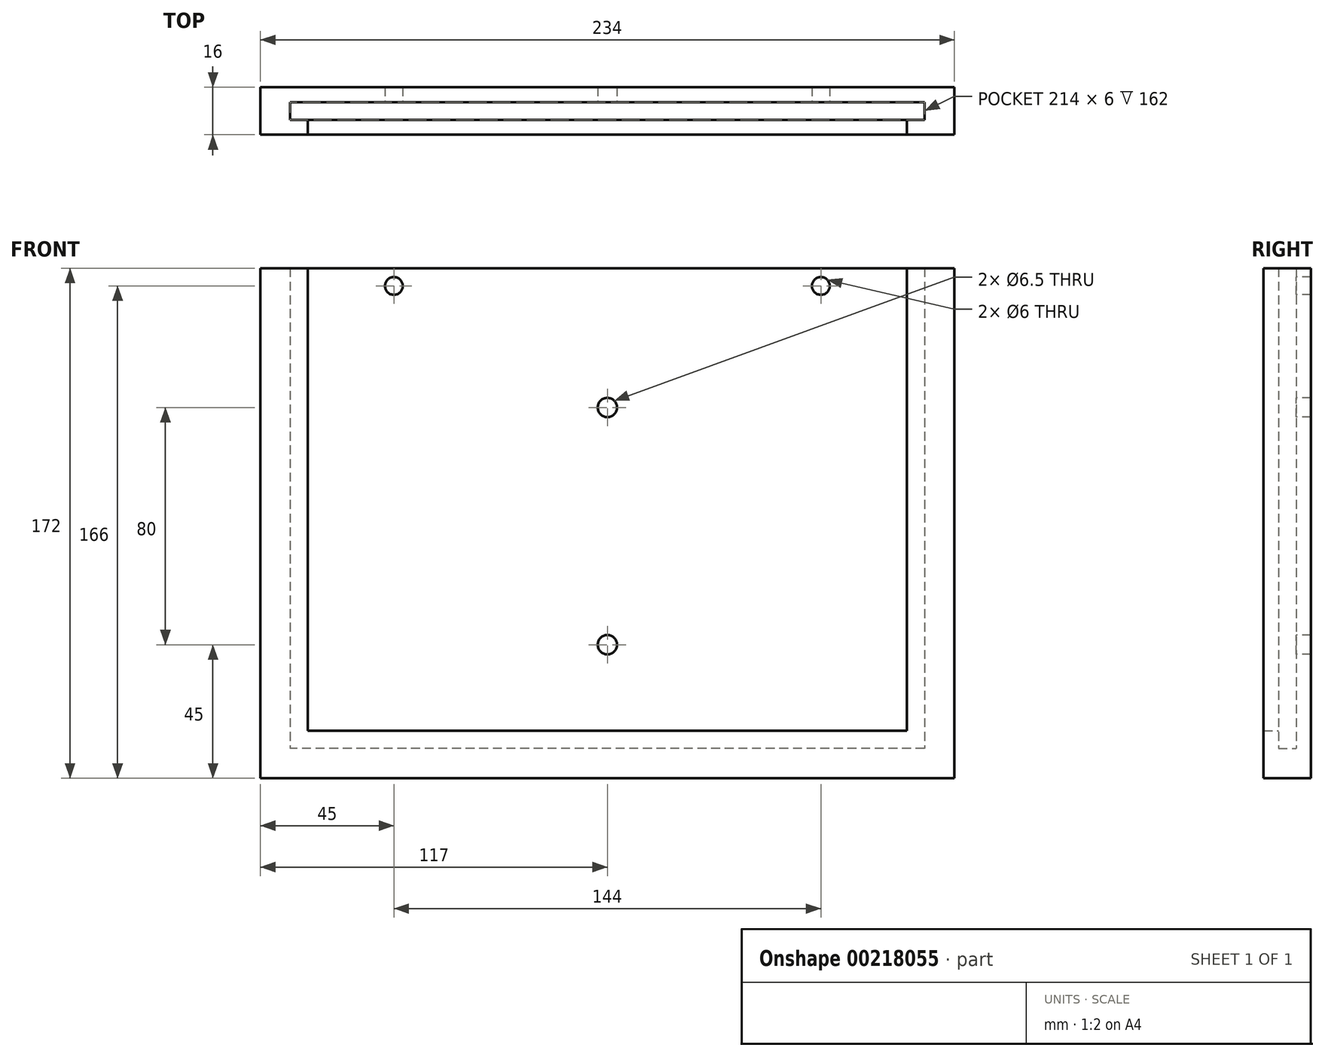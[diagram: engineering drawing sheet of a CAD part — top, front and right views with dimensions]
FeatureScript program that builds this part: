
annotation { "Feature Type Name" : "Feature", "Feature Type Description" : "" }
export const myFeature = defineFeature(function(context is Context, id is Id, definition is map)
    precondition{}
    {
        {
            var Q0;
            Q0=qCreatedBy(makeId("Top.planeOp"),FACE);
            var sketch = newSketch(context, id + "F0", { "sketchPlane" : qUnion([Q0])});
            skLineSegment(sketch, "E0.bottom", {"start": v(-117, 8) * mm, "end": v(117, 8) * mm});
            skLineSegment(sketch, "E0.top", {"start": v(-117, -8) * mm, "end": v(117, -8) * mm});
            skLineSegment(sketch, "E0.left", {"start": v(-117, 8) * mm, "end": v(-117, -8) * mm});
            skLineSegment(sketch, "E0.right", {"start": v(117, 8) * mm, "end": v(117, -8) * mm});
            skPoint(sketch, "E0.middle", {"position": v(0, 0) * mm});
            skLineSegment(sketch, "E1.top", {"start": v(-117, 3) * mm, "end": v(117, 3) * mm});
            skLineSegment(sketch, "E1.left", {"start": v(-117, 8) * mm, "end": v(-117, 3) * mm});
            skLineSegment(sketch, "E1.right", {"start": v(117, 8) * mm, "end": v(117, 3) * mm});
            skLineSegment(sketch, "E2", {"start": v(-107, -8) * mm, "end": v(-107, 8) * mm});
            skLineSegment(sketch, "E3", {"start": v(107, -8) * mm, "end": v(107, 8) * mm});
            skLineSegment(sketch, "E4.bottom", {"start": v(-117, -8) * mm, "end": v(-101, -8) * mm});
            skLineSegment(sketch, "E4.top", {"start": v(-117, -3) * mm, "end": v(-101, -3) * mm});
            skLineSegment(sketch, "E4.left", {"start": v(-117, -8) * mm, "end": v(-117, -3) * mm});
            skLineSegment(sketch, "E4.right", {"start": v(-101, -8) * mm, "end": v(-101, -3) * mm});
            skLineSegment(sketch, "E5.bottom", {"start": v(117, -8) * mm, "end": v(101, -8) * mm});
            skLineSegment(sketch, "E5.top", {"start": v(117, -3) * mm, "end": v(101, -3) * mm});
            skLineSegment(sketch, "E5.left", {"start": v(117, -8) * mm, "end": v(117, -3) * mm});
            skLineSegment(sketch, "E5.right", {"start": v(101, -8) * mm, "end": v(101, -3) * mm});
            skLineSegment(sketch, "E6.bottom", {"start": v(-101, -3) * mm, "end": v(107, -3) * mm});
            skLineSegment(sketch, "E6.top", {"start": v(-101, -8) * mm, "end": v(107, -8) * mm});
            skLineSegment(sketch, "E6.left", {"start": v(-101, -3) * mm, "end": v(-101, -8) * mm});
            skLineSegment(sketch, "E6.right", {"start": v(107, -3) * mm, "end": v(107, -8) * mm});
            skSolve(sketch);
        }
        {
            var Q0;
            {var subQ9=sQuery(id+"F0.wireOp",EDGE,"E6.bottom");Q0=makeQuery(id+"F0.imprint","IMPRINT",FACE,{"disambiguationData":[TD([[makeQuery(id+"F0.imprint","IMPRINT",EDGE,{"derivedFrom":subQ9}),1.0]])]});}
            var Q1;
            {var subQ0=sQuery(id+"F0.wireOp",EDGE,"E2");var subQ1=sQuery(id+"F0.wireOp",EDGE,"E0.bottom");var subQ2=makeQuery(id+"F0.imprint","INTERSECT",VERTEX,{"derivedFrom":[subQ1,subQ0]});Q1=makeQuery(id+"F0.imprint","IMPRINT",FACE,{"disambiguationData":[TD([[makeQuery(id+"F0.imprint","IMPRINT",EDGE,{"disambiguationData":[TD([[subQ2,-1.0]])],"derivedFrom":subQ1}),-1.0]])]});}
            var Q2;
            {var subQ0=sQuery(id+"F0.wireOp",EDGE,"E4.right");Q2=makeQuery(id+"F0.imprint","IMPRINT",FACE,{"disambiguationData":[TD([[makeQuery(id+"F0.imprint","IMPRINT",EDGE,{"derivedFrom":subQ0}),-1.0]])]});}
            var Q3;
            {var subQ0=sQuery(id+"F0.wireOp",EDGE,"E1.top");var subQ1=sQuery(id+"F0.wireOp",EDGE,"E0.left");var subQ2=makeQuery(id+"F0.imprint","INTERSECT",VERTEX,{"derivedFrom":[subQ1,subQ0]});Q3=makeQuery(id+"F0.imprint","IMPRINT",FACE,{"disambiguationData":[TD([[makeQuery(id+"F0.imprint","IMPRINT",EDGE,{"disambiguationData":[TD([[subQ2,-1.0]])],"derivedFrom":subQ1}),1.0]])]});}
            var Q4;
            {var subQ0=sQuery(id+"F0.wireOp",EDGE,"E2");var subQ1=sQuery(id+"F0.wireOp",EDGE,"E0.bottom");var subQ2=makeQuery(id+"F0.imprint","INTERSECT",VERTEX,{"derivedFrom":[subQ1,subQ0]});Q4=makeQuery(id+"F0.imprint","IMPRINT",FACE,{"disambiguationData":[TD([[makeQuery(id+"F0.imprint","IMPRINT",EDGE,{"disambiguationData":[TD([[subQ2,1.0]])],"derivedFrom":subQ1}),-1.0]])]});}
            var Q5;
            {var subQ0=sQuery(id+"F0.wireOp",EDGE,"E0.left");var subQ1=sQuery(id+"F0.wireOp",EDGE,"E0.top");var subQ2=makeQuery(id+"F0.imprint","INTERSECT",VERTEX,{"derivedFrom":[subQ1,subQ0]});Q5=makeQuery(id+"F0.imprint","IMPRINT",FACE,{"disambiguationData":[TD([[makeQuery(id+"F0.imprint","IMPRINT",EDGE,{"disambiguationData":[TD([[subQ2,-1.0]])],"derivedFrom":subQ1}),1.0]])]});}
            var Q6;
            {var subQ0=sQuery(id+"F0.wireOp",EDGE,"E4.right");Q6=makeQuery(id+"F0.imprint","IMPRINT",FACE,{"disambiguationData":[TD([[makeQuery(id+"F0.imprint","IMPRINT",EDGE,{"derivedFrom":subQ0}),1.0]])]});}
            var Q7;
            {var subQ0=sQuery(id+"F0.wireOp",EDGE,"E1.top");var subQ1=sQuery(id+"F0.wireOp",EDGE,"E0.right");var subQ2=makeQuery(id+"F0.imprint","INTERSECT",VERTEX,{"derivedFrom":[subQ1,subQ0]});Q7=makeQuery(id+"F0.imprint","IMPRINT",FACE,{"disambiguationData":[TD([[makeQuery(id+"F0.imprint","IMPRINT",EDGE,{"disambiguationData":[TD([[subQ2,-1.0]])],"derivedFrom":subQ1}),-1.0]])]});}
            var Q8;
            {var subQ0=sQuery(id+"F0.wireOp",EDGE,"E0.right");var subQ1=sQuery(id+"F0.wireOp",EDGE,"E0.bottom");var subQ2=makeQuery(id+"F0.imprint","INTERSECT",VERTEX,{"derivedFrom":[subQ1,subQ0]});Q8=makeQuery(id+"F0.imprint","IMPRINT",FACE,{"disambiguationData":[TD([[makeQuery(id+"F0.imprint","IMPRINT",EDGE,{"disambiguationData":[TD([[subQ2,1.0]])],"derivedFrom":subQ1}),-1.0]])]});}
            var Q9;
            {var subQ3=sQuery(id+"F0.wireOp",EDGE,"E5.right");Q9=makeQuery(id+"F0.imprint","IMPRINT",FACE,{"disambiguationData":[TD([[makeQuery(id+"F0.imprint","IMPRINT",EDGE,{"derivedFrom":subQ3}),-1.0]])]});}
            var Q10;
            {var subQ0=sQuery(id+"F0.wireOp",EDGE,"E3");var subQ1=sQuery(id+"F0.wireOp",EDGE,"E0.top");var subQ2=makeQuery(id+"F0.imprint","INTERSECT",VERTEX,{"derivedFrom":[subQ1,subQ0]});Q10=makeQuery(id+"F0.imprint","IMPRINT",FACE,{"disambiguationData":[TD([[makeQuery(id+"F0.imprint","IMPRINT",EDGE,{"disambiguationData":[TD([[subQ2,-1.0]])],"derivedFrom":subQ1}),1.0]])]});}
            extrude(context, id + "F1", {"entities" : qUnion([Q0, Q1, Q2, Q3, Q4, Q5, Q6, Q7, Q8, Q9, Q10]), "oppositeDirection" : true, "depth" : 10 * mm, "offsetDistance" : 25 * mm});
        }
        {
            var Q0;
            {var subQ0=sQuery(id+"F0.wireOp",EDGE,"E2");var subQ1=sQuery(id+"F0.wireOp",EDGE,"E0.bottom");var subQ2=makeQuery(id+"F0.imprint","INTERSECT",VERTEX,{"derivedFrom":[subQ1,subQ0]});Q0=makeQuery(id+"F0.imprint","IMPRINT",FACE,{"disambiguationData":[TD([[makeQuery(id+"F0.imprint","IMPRINT",EDGE,{"disambiguationData":[TD([[subQ2,-1.0]])],"derivedFrom":subQ1}),-1.0]])]});}
            var Q1;
            {var subQ0=sQuery(id+"F0.wireOp",EDGE,"E2");var subQ1=sQuery(id+"F0.wireOp",EDGE,"E0.bottom");var subQ2=makeQuery(id+"F0.imprint","INTERSECT",VERTEX,{"derivedFrom":[subQ1,subQ0]});Q1=makeQuery(id+"F0.imprint","IMPRINT",FACE,{"disambiguationData":[TD([[makeQuery(id+"F0.imprint","IMPRINT",EDGE,{"disambiguationData":[TD([[subQ2,1.0]])],"derivedFrom":subQ1}),-1.0]])]});}
            var Q2;
            {var subQ0=sQuery(id+"F0.wireOp",EDGE,"E1.top");var subQ1=sQuery(id+"F0.wireOp",EDGE,"E0.left");var subQ2=makeQuery(id+"F0.imprint","INTERSECT",VERTEX,{"derivedFrom":[subQ1,subQ0]});Q2=makeQuery(id+"F0.imprint","IMPRINT",FACE,{"disambiguationData":[TD([[makeQuery(id+"F0.imprint","IMPRINT",EDGE,{"disambiguationData":[TD([[subQ2,-1.0]])],"derivedFrom":subQ1}),1.0]])]});}
            var Q3;
            {var subQ0=sQuery(id+"F0.wireOp",EDGE,"E0.left");var subQ1=sQuery(id+"F0.wireOp",EDGE,"E0.top");var subQ2=makeQuery(id+"F0.imprint","INTERSECT",VERTEX,{"derivedFrom":[subQ1,subQ0]});Q3=makeQuery(id+"F0.imprint","IMPRINT",FACE,{"disambiguationData":[TD([[makeQuery(id+"F0.imprint","IMPRINT",EDGE,{"disambiguationData":[TD([[subQ2,-1.0]])],"derivedFrom":subQ1}),1.0]])]});}
            var Q4;
            {var subQ0=sQuery(id+"F0.wireOp",EDGE,"E0.right");var subQ1=sQuery(id+"F0.wireOp",EDGE,"E0.bottom");var subQ2=makeQuery(id+"F0.imprint","INTERSECT",VERTEX,{"derivedFrom":[subQ1,subQ0]});Q4=makeQuery(id+"F0.imprint","IMPRINT",FACE,{"disambiguationData":[TD([[makeQuery(id+"F0.imprint","IMPRINT",EDGE,{"disambiguationData":[TD([[subQ2,1.0]])],"derivedFrom":subQ1}),-1.0]])]});}
            var Q5;
            {var subQ0=sQuery(id+"F0.wireOp",EDGE,"E1.top");var subQ1=sQuery(id+"F0.wireOp",EDGE,"E0.right");var subQ2=makeQuery(id+"F0.imprint","INTERSECT",VERTEX,{"derivedFrom":[subQ1,subQ0]});Q5=makeQuery(id+"F0.imprint","IMPRINT",FACE,{"disambiguationData":[TD([[makeQuery(id+"F0.imprint","IMPRINT",EDGE,{"disambiguationData":[TD([[subQ2,-1.0]])],"derivedFrom":subQ1}),-1.0]])]});}
            var Q6;
            {var subQ0=sQuery(id+"F0.wireOp",EDGE,"E3");var subQ1=sQuery(id+"F0.wireOp",EDGE,"E0.top");var subQ2=makeQuery(id+"F0.imprint","INTERSECT",VERTEX,{"derivedFrom":[subQ1,subQ0]});Q6=makeQuery(id+"F0.imprint","IMPRINT",FACE,{"disambiguationData":[TD([[makeQuery(id+"F0.imprint","IMPRINT",EDGE,{"disambiguationData":[TD([[subQ2,-1.0]])],"derivedFrom":subQ1}),1.0]])]});}
            var Q7;
            {var subQ3=sQuery(id+"F0.wireOp",EDGE,"E5.right");Q7=makeQuery(id+"F0.imprint","IMPRINT",FACE,{"disambiguationData":[TD([[makeQuery(id+"F0.imprint","IMPRINT",EDGE,{"derivedFrom":subQ3}),-1.0]])]});}
            var Q8;
            {var subQ0=sQuery(id+"F0.wireOp",EDGE,"E4.right");Q8=makeQuery(id+"F0.imprint","IMPRINT",FACE,{"disambiguationData":[TD([[makeQuery(id+"F0.imprint","IMPRINT",EDGE,{"derivedFrom":subQ0}),1.0]])]});}
            extrude(context, id + "F2", {"entities" : qUnion([Q0, Q1, Q2, Q3, Q4, Q5, Q6, Q7, Q8]), "operationType" : NewBodyOperationType.ADD, "depth" : 162 * mm, "offsetDistance" : 25 * mm});
        }
        {
            var Q0;
            {var subQ0=sQuery(id+"F0.wireOp",EDGE,"E4.right");Q0=makeQuery(id+"F0.imprint","IMPRINT",FACE,{"disambiguationData":[TD([[makeQuery(id+"F0.imprint","IMPRINT",EDGE,{"derivedFrom":subQ0}),-1.0]])]});}
            extrude(context, id + "F3", {"entities" : qUnion([Q0]), "operationType" : NewBodyOperationType.ADD, "depth" : 6 * mm, "offsetDistance" : 25 * mm});
        }
        {
            var Q0;
            Q0=makeQuery(id+"F2.opExtrude","SWEPT_FACE",FACE,{"disambiguationData":[OSD([sQuery(id+"F0.wireOp",EDGE,"E1.top")])]});
            var sketch = newSketch(context, id + "F4", { "sketchPlane" : qUnion([Q0])});
            skCircle(sketch, "E7", {"center": v(-72, 156) * mm, "radius": 3 * mm});
            skCircle(sketch, "E8", {"center": v(72, 156) * mm, "radius": 3 * mm});
            skCircle(sketch, "E9", {"center": v(0, 115) * mm, "radius": 3.25 * mm});
            skCircle(sketch, "E10", {"center": v(0, 35) * mm, "radius": 3.25 * mm});
            skSolve(sketch);
        }
        {
            var Q0;
            Q0=makeQuery(id+"F4.imprint","IMPRINT",FACE,{"disambiguationData":[TD([[makeQuery(id+"F4.imprint","IMPRINT",EDGE,{"derivedFrom":sQuery(id+"F4.wireOp",EDGE,"E9")}),1.0]])]});
            var Q1;
            Q1=makeQuery(id+"F4.imprint","IMPRINT",FACE,{"disambiguationData":[TD([[makeQuery(id+"F4.imprint","IMPRINT",EDGE,{"derivedFrom":sQuery(id+"F4.wireOp",EDGE,"E8")}),1.0]])]});
            var Q2;
            Q2=makeQuery(id+"F4.imprint","IMPRINT",FACE,{"disambiguationData":[TD([[makeQuery(id+"F4.imprint","IMPRINT",EDGE,{"derivedFrom":sQuery(id+"F4.wireOp",EDGE,"E10")}),1.0]])]});
            var Q3;
            Q3=makeQuery(id+"F4.imprint","IMPRINT",FACE,{"disambiguationData":[TD([[makeQuery(id+"F4.imprint","IMPRINT",EDGE,{"derivedFrom":sQuery(id+"F4.wireOp",EDGE,"E7")}),1.0]])]});
            var Q4;
            Q4=sQuery(id+"F4.wireOp",EDGE,"E7");
            var Q5;
            Q5=sQuery(id+"F4.wireOp",EDGE,"E9");
            var Q6;
            Q6=sQuery(id+"F4.wireOp",EDGE,"E8");
            var Q7;
            Q7=sQuery(id+"F4.wireOp",EDGE,"E10");
            extrude(context, id + "F5", {"entities" : qUnion([Q0, Q1, Q2, Q3]), "operationType" : NewBodyOperationType.REMOVE, "surfaceEntities" : qUnion([Q4, Q5, Q6, Q7]), "oppositeDirection" : true, "depth" : 25 * mm, "offsetDistance" : 25 * mm});
        }
    });
